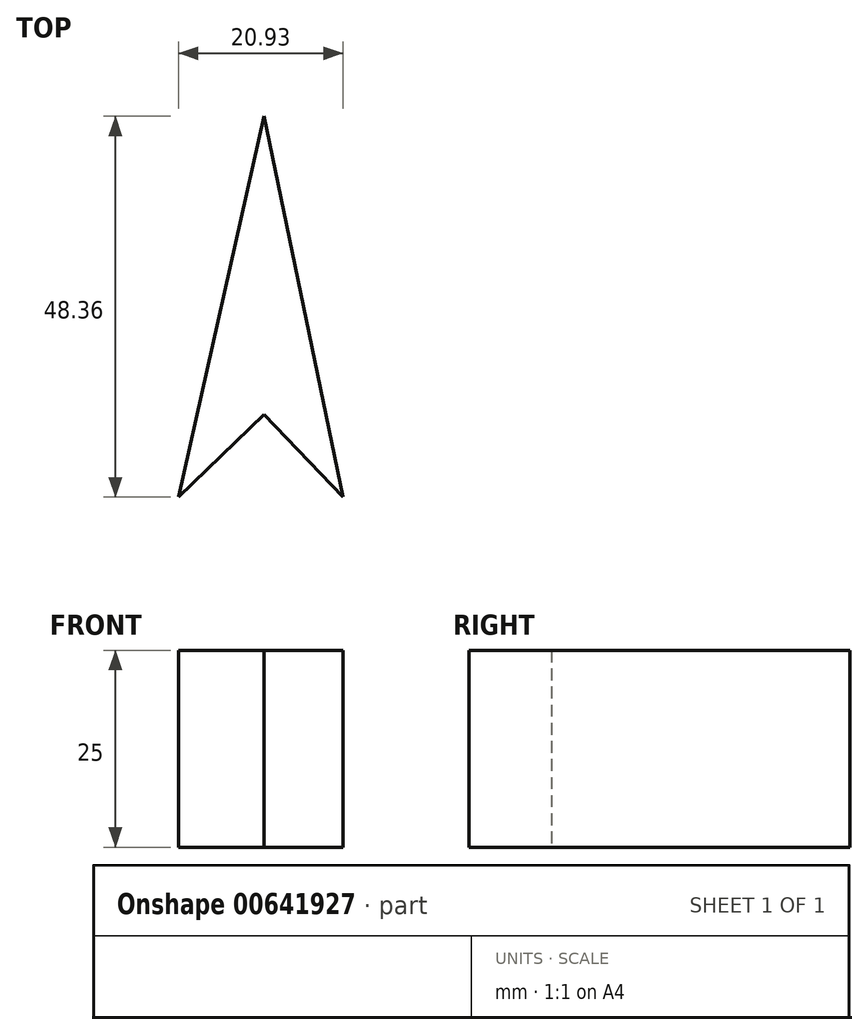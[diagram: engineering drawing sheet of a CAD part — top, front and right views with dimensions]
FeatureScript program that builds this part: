
annotation { "Feature Type Name" : "Feature", "Feature Type Description" : "" }
export const myFeature = defineFeature(function(context is Context, id is Id, definition is map)
    precondition{}
    {
        {
            var Q0;
            Q0=qCreatedBy(makeId("Top.planeOp"),FACE);
            var sketch = newSketch(context, id + "F0", { "sketchPlane" : qUnion([Q0])});
            skCircle(sketch, "E0", {"center": v(0, 0) * mm, "radius": 48.7 * mm});
            skSolve(sketch);
        }
        {
            var Q0;
            Q0=makeQuery(id+"F0.imprint","IMPRINT",FACE,{"disambiguationData":[TD([[makeQuery(id+"F0.imprint","IMPRINT",EDGE,{"derivedFrom":sQuery(id+"F0.wireOp",EDGE,"E0")}),1.0]])]});
            var sketch = newSketch(context, id + "F1", { "sketchPlane" : qUnion([Q0])});
            skLineSegment(sketch, "E1", {"start": v(0, 48.36) * mm, "end": v(-10.88, 0) * mm});
            skLineSegment(sketch, "E2", {"start": v(-10.88, 0) * mm, "end": v(0, 10.46) * mm});
            skLineSegment(sketch, "E3", {"start": v(0, 10.46) * mm, "end": v(10.05, 0) * mm});
            skLineSegment(sketch, "E4", {"start": v(10.05, 0) * mm, "end": v(0, 48.36) * mm});
            skSolve(sketch);
        }
        {
            var Q0;
            Q0=makeQuery(id+"F1.imprint","IMPRINT",FACE,{"disambiguationData":[TD([[makeQuery(id+"F1.imprint","IMPRINT",EDGE,{"derivedFrom":sQuery(id+"F1.wireOp",EDGE,"E1")}),-1.0]])]});
            var sketch = newSketch(context, id + "F2", { "sketchPlane" : qUnion([Q0])});
            skLineSegment(sketch, "E5", {"start": v(-10.88, 0) * mm, "end": v(-37.27, -30.25) * mm});
            skLineSegment(sketch, "E6", {"start": v(0, -12) * mm, "end": v(-37.27, -30.25) * mm});
            skLineSegment(sketch, "E7", {"start": v(-10.88, 0) * mm, "end": v(-10.88, -9.2) * mm});
            skLineSegment(sketch, "E8", {"start": v(-10.88, -9.2) * mm, "end": v(0, -12) * mm});
            skSolve(sketch);
        }
        {
            var Q0;
            Q0=makeQuery(id+"F2.imprint","IMPRINT",FACE,{"disambiguationData":[TD([[makeQuery(id+"F2.imprint","IMPRINT",EDGE,{"derivedFrom":makeQuery(id+"F1.imprint","IMPRINT",EDGE,{"derivedFrom":sQuery(id+"F1.wireOp",EDGE,"E1")})}),1.0]])]});
            extrude(context, id + "F3", {"entities" : qUnion([Q0]), "depth" : 25 * mm, "offsetDistance" : 25 * mm});
        }
    });
